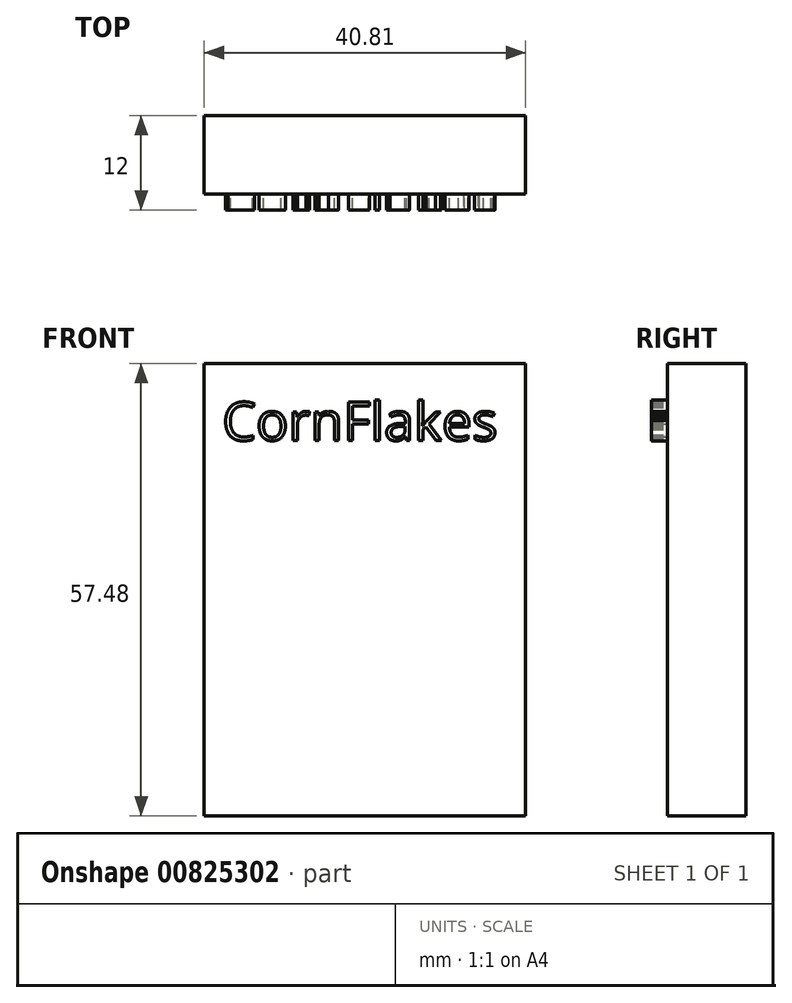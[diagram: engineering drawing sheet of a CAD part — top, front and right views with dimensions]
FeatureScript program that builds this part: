
annotation { "Feature Type Name" : "Feature", "Feature Type Description" : "" }
export const myFeature = defineFeature(function(context is Context, id is Id, definition is map)
    precondition{}
    {
        {
            var Q0;
            Q0=qCreatedBy(makeId("Front.planeOp"),FACE);
            var sketch = newSketch(context, id + "F0", { "sketchPlane" : qUnion([Q0])});
            skLineSegment(sketch, "E0.bottom", {"start": v(-48.14, 63.66) * mm, "end": v(-7.33, 63.66) * mm});
            skLineSegment(sketch, "E0.top", {"start": v(-48.14, 6.18) * mm, "end": v(-7.33, 6.18) * mm});
            skLineSegment(sketch, "E0.left", {"start": v(-48.14, 63.66) * mm, "end": v(-48.14, 6.18) * mm});
            skLineSegment(sketch, "E0.right", {"start": v(-7.33, 63.66) * mm, "end": v(-7.33, 6.18) * mm});
            skSolve(sketch);
        }
        {
            var Q0;
            Q0=makeQuery(id+"F0.imprint","IMPRINT",FACE,{"disambiguationData":[TD([[makeQuery(id+"F0.imprint","IMPRINT",EDGE,{"derivedFrom":sQuery(id+"F0.wireOp",EDGE,"E0.bottom")}),-1.0]])]});
            extrude(context, id + "F1", {"entities" : qUnion([Q0]), "depth" : 10 * mm, "offsetDistance" : 25 * mm});
        }
        {
            var Q0;
            Q0=qCreatedBy(makeId("Front.planeOp"),FACE);
            var sketch = newSketch(context, id + "F2", { "sketchPlane" : qUnion([Q0])});
            skText(sketch, "E1", { "text": "CornFlakes", "fontName": "OpenSans-Regular.ttf"});
            const initialGuessF2  = {"E1": [-0.04584, 0.05389, 1, 0, 0.00489]};
            skSetInitialGuess(sketch, initialGuessF2);
            skSolve(sketch);
        }
        {
            var Q0;
            Q0 = qSketchRegion(id + "F2", true);
            extrude(context, id + "F3", {"entities" : qUnion([Q0]), "operationType" : NewBodyOperationType.ADD, "depth" : 12 * mm, "offsetDistance" : 25 * mm});
        }
    });
